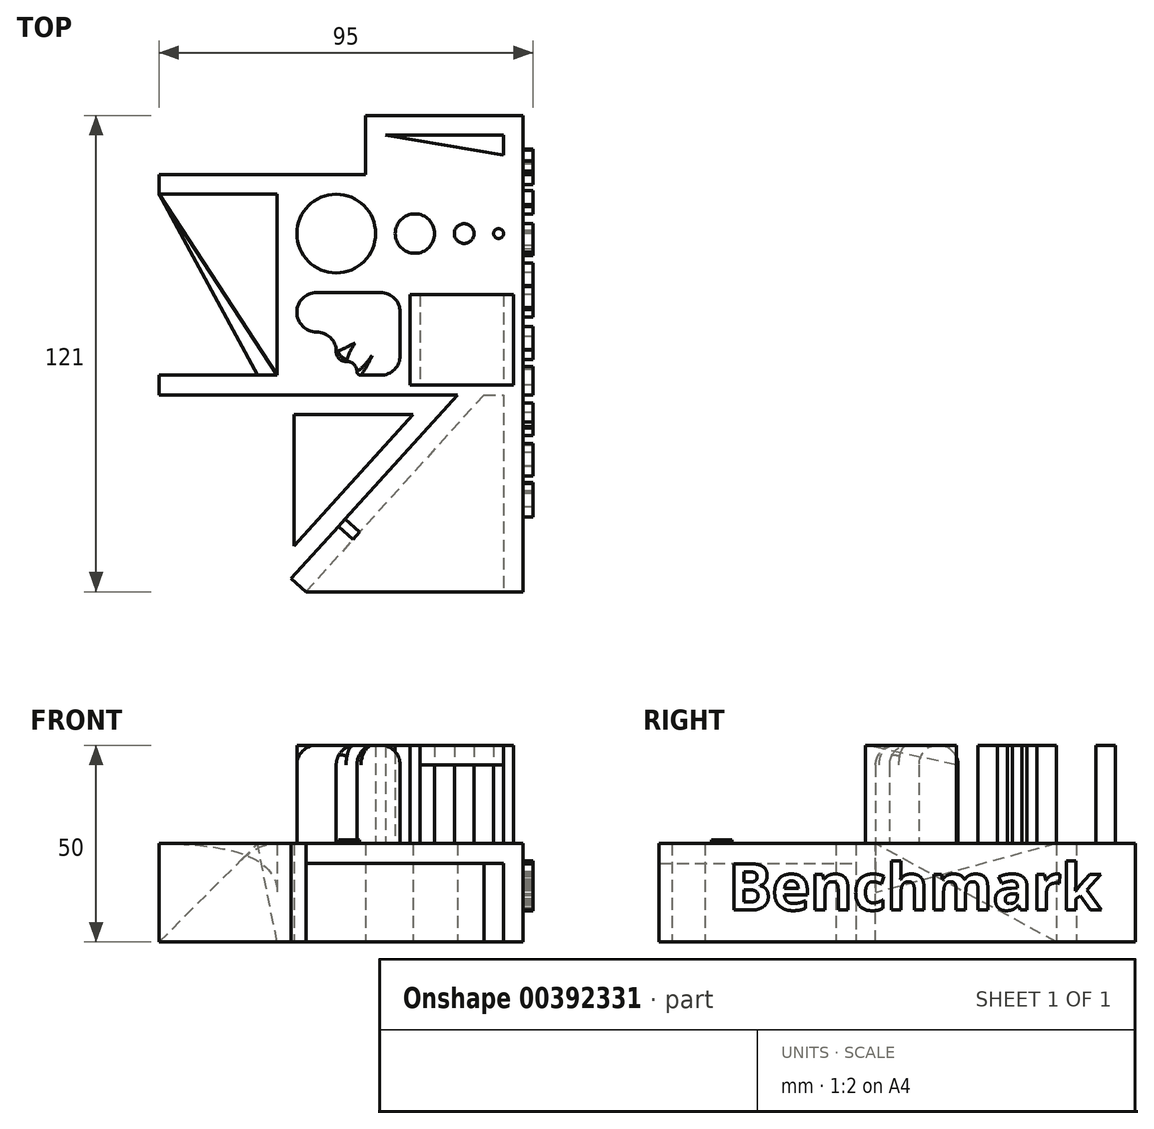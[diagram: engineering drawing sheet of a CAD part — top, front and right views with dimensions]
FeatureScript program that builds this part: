
annotation { "Feature Type Name" : "Feature", "Feature Type Description" : "" }
export const myFeature = defineFeature(function(context is Context, id is Id, definition is map)
    precondition{}
    {
        {
            var Q0;
            Q0=qCreatedBy(makeId("Top.planeOp"),FACE);
            var sketch = newSketch(context, id + "F0", { "sketchPlane" : qUnion([Q0])});
            skLineSegment(sketch, "E0.bottom", {"start": v(31.25, 28) * mm, "end": v(-31.25, 28) * mm});
            skLineSegment(sketch, "E0.top", {"start": v(31.25, -28) * mm, "end": v(-31.25, -28) * mm});
            skLineSegment(sketch, "E0.left", {"start": v(31.25, 28) * mm, "end": v(31.25, -28) * mm});
            skLineSegment(sketch, "E0.right", {"start": v(-31.25, 28) * mm, "end": v(-31.25, -28) * mm});
            skLineSegment(sketch, "E1.bottom", {"start": v(-31.25, 28) * mm, "end": v(-61.25, 28) * mm});
            skLineSegment(sketch, "E1.top", {"start": v(-31.25, 23) * mm, "end": v(-61.25, 23) * mm});
            skLineSegment(sketch, "E1.left", {"start": v(-31.25, 28) * mm, "end": v(-31.25, 23) * mm});
            skLineSegment(sketch, "E1.right", {"start": v(-61.25, 28) * mm, "end": v(-61.25, 23) * mm});
            skLineSegment(sketch, "E2.bottom", {"start": v(-31.25, -28) * mm, "end": v(-61.25, -28) * mm});
            skLineSegment(sketch, "E2.top", {"start": v(-31.25, -23) * mm, "end": v(-61.25, -23) * mm});
            skLineSegment(sketch, "E2.left", {"start": v(-31.25, -28) * mm, "end": v(-31.25, -23) * mm});
            skLineSegment(sketch, "E2.right", {"start": v(-61.25, -28) * mm, "end": v(-61.25, -23) * mm});
            skCircle(sketch, "E3", {"center": v(-16.25, 13) * mm, "radius": 10 * mm});
            skCircle(sketch, "E4", {"center": v(3.75, 13) * mm, "radius": 5 * mm});
            skCircle(sketch, "E5", {"center": v(16.25, 13) * mm, "radius": 2.5 * mm});
            skCircle(sketch, "E6", {"center": v(25, 13) * mm, "radius": 1.25 * mm});
            skLineSegment(sketch, "E7", {"start": v(-31.25, 13) * mm, "end": v(31.25, 13) * mm, "construction": true});
            skLineSegment(sketch, "E8", {"start": v(-26.25, -7) * mm, "end": v(-26.25, -7) * mm});
            skLineSegment(sketch, "E9", {"start": v(-21.25, -12) * mm, "end": v(-21.25, -12) * mm});
            skLineSegment(sketch, "E10", {"start": v(-16.25, -17) * mm, "end": v(-16.25, -17) * mm});
            skLineSegment(sketch, "E11", {"start": v(-13.75, -19.5) * mm, "end": v(-13.5, -19.5) * mm});
            skLineSegment(sketch, "E12", {"start": v(-11, -22) * mm, "end": v(-11, -22) * mm});
            skLineSegment(sketch, "E13", {"start": v(-10, -23) * mm, "end": v(-5, -23) * mm});
            skLineSegment(sketch, "E14", {"start": v(0, -18) * mm, "end": v(0, -7) * mm});
            skLineSegment(sketch, "E15", {"start": v(-5, -2) * mm, "end": v(-21.25, -2) * mm});
            skPoint(sketch, "E16.visualSharp", {"position": v(-26.25, -12) * mm});
            skArc(sketch, "E16.filletArc", {"start": v(-26.25, -7) * mm, "mid": v(-24.79, -10.54) * mm, "end": v(-21.25, -12) * mm});
            skPoint(sketch, "E17.visualSharp", {"position": v(-16.25, -12) * mm});
            skArc(sketch, "E17.filletArc", {"start": v(-16.25, -17) * mm, "mid": v(-17.71, -13.46) * mm, "end": v(-21.25, -12) * mm});
            skPoint(sketch, "E18.visualSharp", {"position": v(-16.25, -19.5) * mm});
            skArc(sketch, "E18.filletArc", {"start": v(-16.25, -17) * mm, "mid": v(-15.52, -18.77) * mm, "end": v(-13.75, -19.5) * mm});
            skPoint(sketch, "E19.visualSharp", {"position": v(-11, -19.5) * mm});
            skArc(sketch, "E19.filletArc", {"start": v(-11, -22) * mm, "mid": v(-11.73, -20.23) * mm, "end": v(-13.5, -19.5) * mm});
            skPoint(sketch, "E20.visualSharp", {"position": v(-11, -23) * mm});
            skArc(sketch, "E20.filletArc", {"start": v(-11, -22) * mm, "mid": v(-10.7, -22.7) * mm, "end": v(-10, -23) * mm});
            skPoint(sketch, "E21.visualSharp", {"position": v(-26.25, -2) * mm});
            skArc(sketch, "E21.filletArc", {"start": v(-21.25, -2) * mm, "mid": v(-24.79, -3.46) * mm, "end": v(-26.25, -7) * mm});
            skPoint(sketch, "E22.visualSharp", {"position": v(0, -2) * mm});
            skArc(sketch, "E22.filletArc", {"start": v(0, -7) * mm, "mid": v(-1.46, -3.46) * mm, "end": v(-5, -2) * mm});
            skPoint(sketch, "E23.visualSharp", {"position": v(0, -23) * mm});
            skArc(sketch, "E23.filletArc", {"start": v(-5, -23) * mm, "mid": v(-1.46, -21.54) * mm, "end": v(0, -18) * mm});
            skLineSegment(sketch, "E24.bottom", {"start": v(31.25, -28) * mm, "end": v(26.25, -28) * mm});
            skLineSegment(sketch, "E24.top", {"start": v(31.25, -78) * mm, "end": v(26.25, -78) * mm});
            skLineSegment(sketch, "E24.left", {"start": v(31.25, -28) * mm, "end": v(31.25, -78) * mm});
            skLineSegment(sketch, "E24.right", {"start": v(26.25, -28) * mm, "end": v(26.25, -78) * mm});
            skLineSegment(sketch, "E25", {"start": v(21.25, -28) * mm, "end": v(-23.96, -78) * mm});
            skLineSegment(sketch, "E26", {"start": v(-23.96, -78) * mm, "end": v(-27.67, -74.65) * mm});
            skLineSegment(sketch, "E27", {"start": v(-27.67, -74.65) * mm, "end": v(14.5, -28) * mm});
            skLineSegment(sketch, "E28", {"start": v(-31.25, 0) * mm, "end": v(31.25, 0) * mm, "construction": true});
            skLineSegment(sketch, "E29", {"start": v(0, 28) * mm, "end": v(0, -28) * mm, "construction": true});
            skLineSegment(sketch, "E30.bottom", {"start": v(2.5, -2.5) * mm, "end": v(5, -2.5) * mm});
            skLineSegment(sketch, "E30.top", {"start": v(2.5, -25.5) * mm, "end": v(5, -25.5) * mm});
            skLineSegment(sketch, "E30.left", {"start": v(2.5, -2.5) * mm, "end": v(2.5, -25.5) * mm});
            skLineSegment(sketch, "E30.right", {"start": v(5, -2.5) * mm, "end": v(5, -25.5) * mm});
            skLineSegment(sketch, "E31.bottom", {"start": v(26.25, -2.5) * mm, "end": v(28.75, -2.5) * mm});
            skLineSegment(sketch, "E31.top", {"start": v(26.25, -25.5) * mm, "end": v(28.75, -25.5) * mm});
            skLineSegment(sketch, "E31.left", {"start": v(26.25, -2.5) * mm, "end": v(26.25, -25.5) * mm});
            skLineSegment(sketch, "E31.right", {"start": v(28.75, -2.5) * mm, "end": v(28.75, -25.5) * mm});
            skLineSegment(sketch, "E32", {"start": v(3.25, -33) * mm, "end": v(-26.94, -66.38) * mm});
            skLineSegment(sketch, "E33", {"start": v(-26.94, -66.38) * mm, "end": v(-26.94, -33) * mm});
            skLineSegment(sketch, "E34", {"start": v(-26.94, -33) * mm, "end": v(3.25, -33) * mm});
            skLineSegment(sketch, "E35", {"start": v(-15.67, -61.38) * mm, "end": v(-11.96, -64.73) * mm});
            skLineSegment(sketch, "E36", {"start": v(-11.96, -64.73) * mm, "end": v(-10.29, -62.88) * mm});
            skLineSegment(sketch, "E37", {"start": v(-10.29, -62.88) * mm, "end": v(-14, -59.52) * mm});
            skLineSegment(sketch, "E38.bottom", {"start": v(31.25, 28) * mm, "end": v(-8.75, 28) * mm});
            skLineSegment(sketch, "E38.top", {"start": v(31.25, 43) * mm, "end": v(-8.75, 43) * mm});
            skLineSegment(sketch, "E38.left", {"start": v(31.25, 28) * mm, "end": v(31.25, 43) * mm});
            skLineSegment(sketch, "E38.right", {"start": v(-8.75, 28) * mm, "end": v(-8.75, 43) * mm});
            skLineSegment(sketch, "E39", {"start": v(26.25, 38) * mm, "end": v(-3.75, 38) * mm});
            skLineSegment(sketch, "E40", {"start": v(-3.75, 38) * mm, "end": v(26.25, 33) * mm});
            skLineSegment(sketch, "E41", {"start": v(26.25, 33) * mm, "end": v(26.25, 38) * mm});
            skSolve(sketch);
        }
        {
            var Q0;
            Q0 = qSketchRegion(id + "F0", true);
            extrude(context, id + "F1", {"entities" : qUnion([Q0]), "depth" : 25 * mm});
        }
        {
            var Q0;
            Q0=makeQuery(id+"F1.opExtrude","SWEPT_FACE",FACE,{"disambiguationData":[OSD([sQuery(id+"F0.wireOp",EDGE,"E1.top")])]});
            var sketch = newSketch(context, id + "F2", { "sketchPlane" : qUnion([Q0])});
            skLineSegment(sketch, "E42.bottom", {"start": v(-31.25, 25) * mm, "end": v(-61.25, 25) * mm});
            skLineSegment(sketch, "E42.top", {"start": v(-31.25, 0) * mm, "end": v(-61.25, 0) * mm});
            skLineSegment(sketch, "E42.left", {"start": v(-31.25, 25) * mm, "end": v(-31.25, 0) * mm});
            skLineSegment(sketch, "E42.right", {"start": v(-61.25, 25) * mm, "end": v(-61.25, 0) * mm});
            skSolve(sketch);
        }
        {
            var Q0;
            Q0=makeQuery(id+"F1.opExtrude","SWEPT_FACE",FACE,{"disambiguationData":[OSD([sQuery(id+"F0.wireOp",EDGE,"E2.top")])]});
            var sketch = newSketch(context, id + "F3", { "sketchPlane" : qUnion([Q0])});
            skLineSegment(sketch, "E43", {"start": v(31.25, 25) * mm, "end": v(31.25, 0) * mm});
            skLineSegment(sketch, "E44", {"start": v(31.25, 0) * mm, "end": v(36.25, 25) * mm});
            skLineSegment(sketch, "E45", {"start": v(36.25, 25) * mm, "end": v(31.25, 25) * mm});
            skSolve(sketch);
        }
        {
            var Q1;
            Q1 = qSketchRegion(id + "F2", true);
            var Q2;
            Q2 = qSketchRegion(id + "F3", true);
            loft(context, id + "F4", {"operationType" : NewBodyOperationType.ADD, "sheetProfilesArray" : [{ "sheetProfileEntities" : qUnion([Q1]) }, { "sheetProfileEntities" : qUnion([Q2]) }]});
        }
        {
            var Q0;
            Q0=makeQuery(id+"F0.imprint","IMPRINT",FACE,{"disambiguationData":[TD([[makeQuery(id+"F0.imprint","IMPRINT",EDGE,{"derivedFrom":sQuery(id+"F0.wireOp",EDGE,"E3")}),1.0]])]});
            extrude(context, id + "F5", {"entities" : qUnion([Q0]), "operationType" : NewBodyOperationType.ADD, "depth" : 50 * mm});
        }
        {
            var Q0;
            Q0=makeQuery(id+"F0.imprint","IMPRINT",FACE,{"disambiguationData":[TD([[makeQuery(id+"F0.imprint","IMPRINT",EDGE,{"derivedFrom":sQuery(id+"F0.wireOp",EDGE,"E4")}),1.0]])]});
            extrude(context, id + "F6", {"entities" : qUnion([Q0]), "operationType" : NewBodyOperationType.ADD, "depth" : 50 * mm});
        }
        {
            var Q0;
            Q0=makeQuery(id+"F0.imprint","IMPRINT",FACE,{"disambiguationData":[TD([[makeQuery(id+"F0.imprint","IMPRINT",EDGE,{"derivedFrom":sQuery(id+"F0.wireOp",EDGE,"E5")}),1.0]])]});
            extrude(context, id + "F7", {"entities" : qUnion([Q0]), "operationType" : NewBodyOperationType.ADD, "depth" : 50 * mm});
        }
        {
            var Q0;
            Q0=makeQuery(id+"F0.imprint","IMPRINT",FACE,{"disambiguationData":[TD([[makeQuery(id+"F0.imprint","IMPRINT",EDGE,{"derivedFrom":sQuery(id+"F0.wireOp",EDGE,"E6")}),1.0]])]});
            extrude(context, id + "F8", {"entities" : qUnion([Q0]), "operationType" : NewBodyOperationType.ADD, "depth" : 50 * mm});
        }
        {
            var Q0;
            Q0=makeQuery(id+"F0.imprint","IMPRINT",FACE,{"disambiguationData":[TD([[makeQuery(id+"F0.imprint","IMPRINT",EDGE,{"derivedFrom":sQuery(id+"F0.wireOp",EDGE,"E13")}),1.0]])]});
            extrude(context, id + "F9", {"entities" : qUnion([Q0]), "operationType" : NewBodyOperationType.ADD, "depth" : 50 * mm});
        }
        {
            var Q0;
            Q0=makeQuery(id+"F9.opExtrude","CAP_EDGE",EDGE,{"disambiguationData":[OSD([sQuery(id+"F0.wireOp",EDGE,"E13")])],"isStart":false});
            fillet(context, id + "F10", {"entities" : qUnion([Q0]), "radius" : 5 * mm, "tangentPropagation" : true, "allowEdgeOverflow" : false});
        }
        {
            var Q0;
            Q0=makeQuery(id+"F1.opExtrude","SWEPT_FACE",FACE,{"disambiguationData":[OSD([sQuery(id+"F0.wireOp",EDGE,"E25")])]});
            var sketch = newSketch(context, id + "F11", { "sketchPlane" : qUnion([Q0])});
            skLineSegment(sketch, "E46.bottom", {"start": v(-73.93, 25) * mm, "end": v(-6.52, 25) * mm});
            skLineSegment(sketch, "E46.top", {"start": v(-73.93, 20) * mm, "end": v(-6.52, 20) * mm});
            skLineSegment(sketch, "E46.left", {"start": v(-73.93, 25) * mm, "end": v(-73.93, 20) * mm});
            skLineSegment(sketch, "E46.right", {"start": v(-6.52, 25) * mm, "end": v(-6.52, 20) * mm});
            skSolve(sketch);
        }
        {
            var Q0;
            Q0=makeQuery(id+"F1.opExtrude","SWEPT_FACE",FACE,{"disambiguationData":[OSD([sQuery(id+"F0.wireOp",EDGE,"E24.right")])]});
            var sketch = newSketch(context, id + "F12", { "sketchPlane" : qUnion([Q0])});
            skLineSegment(sketch, "E47.bottom", {"start": v(28, 25) * mm, "end": v(78, 25) * mm});
            skLineSegment(sketch, "E47.top", {"start": v(28, 20) * mm, "end": v(78, 20) * mm});
            skLineSegment(sketch, "E47.left", {"start": v(28, 25) * mm, "end": v(28, 20) * mm});
            skLineSegment(sketch, "E47.right", {"start": v(78, 25) * mm, "end": v(78, 20) * mm});
            skSolve(sketch);
        }
        {
            var Q1;
            Q1 = qSketchRegion(id + "F11", true);
            var Q2;
            Q2 = qSketchRegion(id + "F12", true);
            loft(context, id + "F13", {"operationType" : NewBodyOperationType.ADD, "sheetProfilesArray" : [{ "sheetProfileEntities" : qUnion([Q1]) }, { "sheetProfileEntities" : qUnion([Q2]) }]});
        }
        {
            var Q0;
            Q0=makeQuery(id+"F1.opExtrude","SWEPT_FACE",FACE,{"disambiguationData":[OSD([sQuery(id+"F0.wireOp",EDGE,"E0.left"),sQuery(id+"F0.wireOp",EDGE,"E24.left")])]});
            var sketch = newSketch(context, id + "F14", { "sketchPlane" : qUnion([Q0])});
            skText(sketch, "E48", { "text": "Benchmark", "fontName": "OpenSans-Bold.ttf"});
            const initialGuessF14  = {"E48": [-0.06045, 0.00812, 1, 0, 0.01188]};
            skSetInitialGuess(sketch, initialGuessF14);
            skSolve(sketch);
        }
        {
            var Q0;
            Q0 = qSketchRegion(id + "F14", true);
            extrude(context, id + "F15", {"entities" : qUnion([Q0]), "operationType" : NewBodyOperationType.ADD, "depth" : 2.5 * mm});
        }
        {
            var Q0;
            Q0=makeQuery(id+"F0.imprint","IMPRINT",FACE,{"disambiguationData":[TD([[makeQuery(id+"F0.imprint","IMPRINT",EDGE,{"derivedFrom":sQuery(id+"F0.wireOp",EDGE,"E30.bottom")}),-1.0]])]});
            extrude(context, id + "F16", {"entities" : qUnion([Q0]), "operationType" : NewBodyOperationType.ADD, "depth" : 50 * mm});
        }
        {
            var Q0;
            Q0=makeQuery(id+"F0.imprint","IMPRINT",FACE,{"disambiguationData":[TD([[makeQuery(id+"F0.imprint","IMPRINT",EDGE,{"derivedFrom":sQuery(id+"F0.wireOp",EDGE,"E31.bottom")}),-1.0]])]});
            extrude(context, id + "F17", {"entities" : qUnion([Q0]), "operationType" : NewBodyOperationType.ADD, "depth" : 50 * mm});
        }
        {
            var Q0;
            Q0=makeQuery(id+"F16.opExtrude","SWEPT_FACE",FACE,{"disambiguationData":[OSD([sQuery(id+"F0.wireOp",EDGE,"E30.right")])]});
            var sketch = newSketch(context, id + "F18", { "sketchPlane" : qUnion([Q0])});
            skLineSegment(sketch, "E49", {"start": v(-25.5, 50) * mm, "end": v(-2.5, 50) * mm});
            skLineSegment(sketch, "E50", {"start": v(-2.5, 50) * mm, "end": v(-2.5, 45) * mm});
            skLineSegment(sketch, "E51", {"start": v(-2.5, 45) * mm, "end": v(-25.5, 50) * mm});
            skSolve(sketch);
        }
        {
            var Q0;
            Q0=makeQuery(id+"F17.opExtrude","SWEPT_FACE",FACE,{"disambiguationData":[OSD([sQuery(id+"F0.wireOp",EDGE,"E31.left")])]});
            var sketch = newSketch(context, id + "F19", { "sketchPlane" : qUnion([Q0])});
            skLineSegment(sketch, "E52", {"start": v(2.5, 50) * mm, "end": v(2.5, 45) * mm});
            skLineSegment(sketch, "E53", {"start": v(2.5, 45) * mm, "end": v(25.5, 50) * mm});
            skLineSegment(sketch, "E54", {"start": v(25.5, 50) * mm, "end": v(2.5, 50) * mm});
            skSolve(sketch);
        }
        {
            var Q1;
            Q1 = qSketchRegion(id + "F18", true);
            var Q2;
            Q2 = qSketchRegion(id + "F19", true);
            loft(context, id + "F20", {"operationType" : NewBodyOperationType.ADD, "sheetProfilesArray" : [{ "sheetProfileEntities" : qUnion([Q1]) }, { "sheetProfileEntities" : qUnion([Q2]) }]});
        }
        {
            var Q0;
            {var subQ0=sQuery(id+"F0.wireOp",EDGE,"E35");Q0=makeQuery(id+"F0.imprint","IMPRINT",FACE,{"disambiguationData":[TD([[makeQuery(id+"F0.imprint","IMPRINT",EDGE,{"derivedFrom":subQ0}),1.0]])]});}
            extrude(context, id + "F21", {"entities" : qUnion([Q0]), "operationType" : NewBodyOperationType.ADD, "depth" : 26 * mm});
        }
        {
            var Q0;
            Q0=makeQuery(id+"F0.imprint","IMPRINT",FACE,{"disambiguationData":[TD([[makeQuery(id+"F0.imprint","IMPRINT",EDGE,{"derivedFrom":sQuery(id+"F0.wireOp",EDGE,"E39")}),1.0]])]});
            extrude(context, id + "F22", {"entities" : qUnion([Q0]), "operationType" : NewBodyOperationType.ADD, "depth" : 50 * mm});
        }
    });
